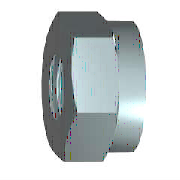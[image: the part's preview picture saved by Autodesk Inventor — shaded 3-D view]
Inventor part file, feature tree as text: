
AUTODESK INVENTOR PART (.ipt)
format: ipt  version: 2021.2 (Build 252289000, 289)  size: 179,712 bytes
history: native  units: mm (DEFAULTED — no unit token found)
features: sketch x4, extrude x2, other x2, hole x1, plane x1
ambient origin geometry x7: Origin, YZ Plane, XZ Plane, X Axis, Y Axis, Z Axis, Center Point
bodies: Solid1 (feature_tree)
feature tree (10):
  extrude  "Базовый элемент"  Depth=8.082904mm
  extrude  "Кольцо"  Depth=2.9mm
  other  "Фаска1"
  hole  "Резьба"  [1 undecoded]
  other  "Work Axis1"
  plane  "Work Plane1"
  sketch  "Эскиз1"
  sketch  "Эскиз3"
  sketch  "Эскиз2"
  sketch  "Эскиз4"
note: 1 required parameter value undecoded (feature->parameter linkage not recoverable at this tier; creation-order binding heuristic only, values carry confidence <= 0.55)
